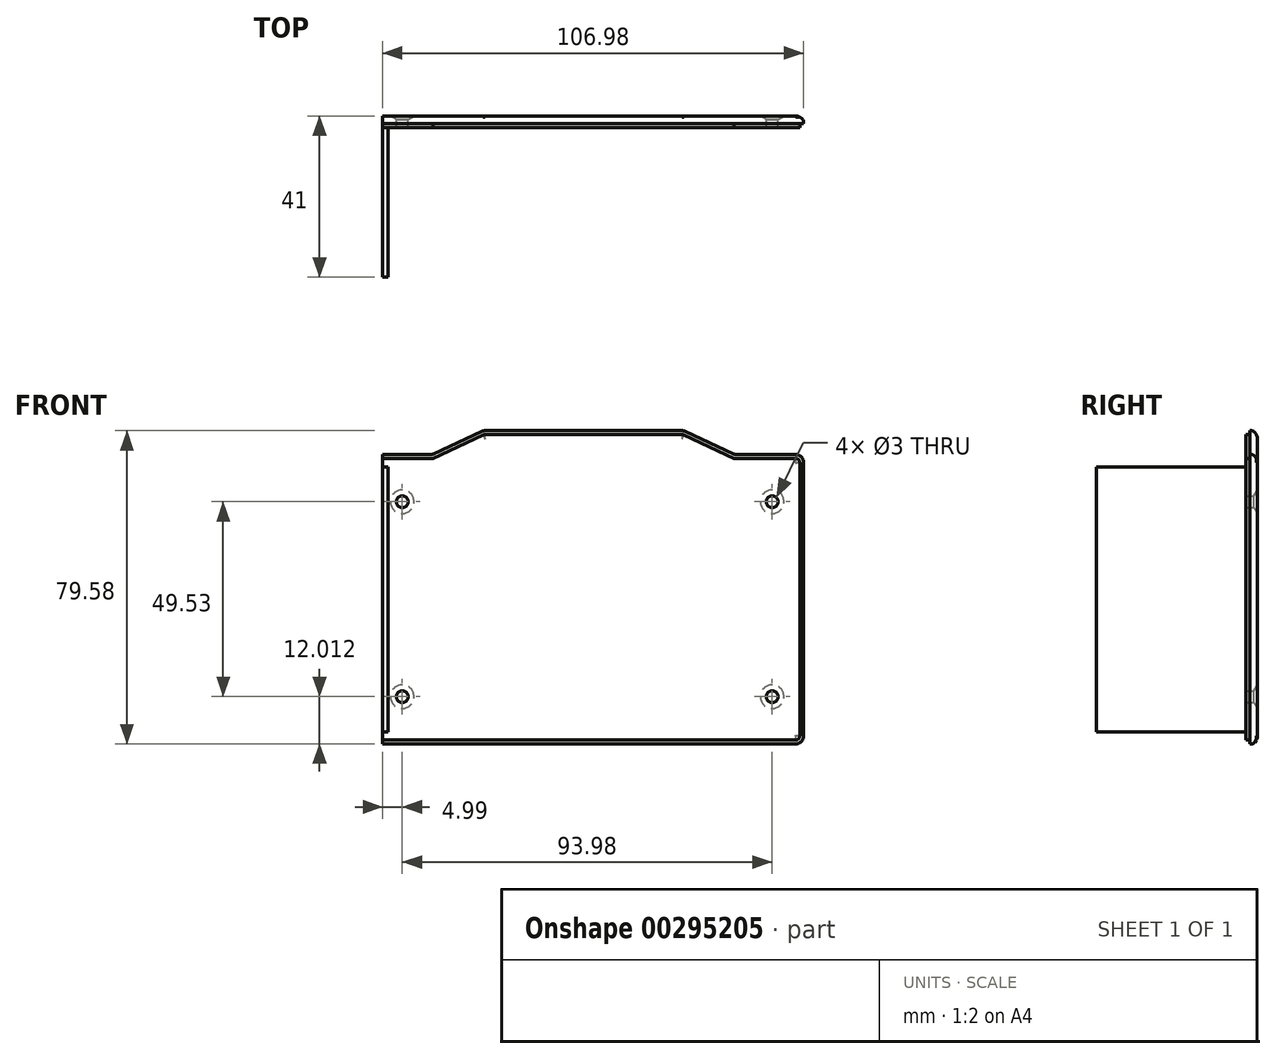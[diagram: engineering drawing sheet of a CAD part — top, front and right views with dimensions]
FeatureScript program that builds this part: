
annotation { "Feature Type Name" : "Feature", "Feature Type Description" : "" }
export const myFeature = defineFeature(function(context is Context, id is Id, definition is map)
    precondition{}
    {
        {
            var Q0;
            Q0=qCreatedBy(makeId("Front.planeOp"),FACE);
            var sketch = newSketch(context, id + "F0", { "sketchPlane" : qUnion([Q0])});
            skLineSegment(sketch, "E0", {"start": v(-120.92, -2) * mm, "end": v(-120.92, -71.52) * mm});
            skLineSegment(sketch, "E1", {"start": v(-118.92, -73.52) * mm, "end": v(-2, -73.52) * mm});
            skLineSegment(sketch, "E2", {"start": v(0, -71.52) * mm, "end": v(0, -2) * mm});
            skLineSegment(sketch, "E3", {"start": v(-81.83, 5.87) * mm, "end": v(-94.02, 0.19) * mm});
            skLineSegment(sketch, "E4", {"start": v(-94.87, 0) * mm, "end": v(-118.92, 0) * mm});
            skLineSegment(sketch, "E5", {"start": v(-2, 0) * mm, "end": v(-16.98, 0) * mm});
            skLineSegment(sketch, "E6", {"start": v(-17.83, 0.19) * mm, "end": v(-30.02, 5.87) * mm});
            skLineSegment(sketch, "E7", {"start": v(-30.87, 6.06) * mm, "end": v(-80.98, 6.06) * mm});
            skPoint(sketch, "E8.visualSharp", {"position": v(0, 0) * mm});
            skArc(sketch, "E8.filletArc", {"start": v(0, -2) * mm, "mid": v(-0.59, -0.59) * mm, "end": v(-2, 0) * mm});
            skPoint(sketch, "E9.visualSharp", {"position": v(-120.92, 0) * mm});
            skArc(sketch, "E9.filletArc", {"start": v(-118.92, 0) * mm, "mid": v(-120.33, -0.59) * mm, "end": v(-120.92, -2) * mm});
            skPoint(sketch, "E10.visualSharp", {"position": v(-120.92, -73.52) * mm});
            skArc(sketch, "E10.filletArc", {"start": v(-120.92, -71.52) * mm, "mid": v(-120.33, -72.93) * mm, "end": v(-118.92, -73.52) * mm});
            skPoint(sketch, "E11.visualSharp", {"position": v(0, -73.52) * mm});
            skArc(sketch, "E11.filletArc", {"start": v(-2, -73.52) * mm, "mid": v(-0.59, -72.93) * mm, "end": v(0, -71.52) * mm});
            skPoint(sketch, "E12.visualSharp", {"position": v(-17.42, 0) * mm});
            skArc(sketch, "E12.filletArc", {"start": v(-17.83, 0.19) * mm, "mid": v(-17.41, 0.05) * mm, "end": v(-16.98, 0) * mm});
            skPoint(sketch, "E13.visualSharp", {"position": v(-30.42, 6.06) * mm});
            skArc(sketch, "E13.filletArc", {"start": v(-30.02, 5.87) * mm, "mid": v(-30.43, 6.01) * mm, "end": v(-30.87, 6.06) * mm});
            skPoint(sketch, "E14.visualSharp", {"position": v(-81.42, 6.06) * mm});
            skArc(sketch, "E14.filletArc", {"start": v(-80.98, 6.06) * mm, "mid": v(-81.41, 6.01) * mm, "end": v(-81.83, 5.87) * mm});
            skPoint(sketch, "E15.visualSharp", {"position": v(-94.42, 0) * mm});
            skArc(sketch, "E15.filletArc", {"start": v(-94.87, 0) * mm, "mid": v(-94.43, 0.05) * mm, "end": v(-94.02, 0.19) * mm});
            skCircle(sketch, "E16", {"center": v(-101.99, -11.98) * mm, "radius": 1.5 * mm});
            skCircle(sketch, "E17", {"center": v(-101.99, -61.5) * mm, "radius": 1.5 * mm});
            skLineSegment(sketch, "E18", {"start": v(-101.99, -11.98) * mm, "end": v(3.2, -11.98) * mm, "construction": true});
            skLineSegment(sketch, "E19", {"start": v(-101.99, -61.5) * mm, "end": v(0.7, -61.5) * mm, "construction": true});
            skCircle(sketch, "E20", {"center": v(-8, -61.5) * mm, "radius": 1.5 * mm});
            skCircle(sketch, "E21", {"center": v(-8, -11.98) * mm, "radius": 1.5 * mm});
            skSolve(sketch);
        }
        {
            var Q0;
            Q0=makeQuery(id+"F0.imprint","IMPRINT",FACE,{"disambiguationData":[TD([[makeQuery(id+"F0.imprint","IMPRINT",EDGE,{"derivedFrom":sQuery(id+"F0.wireOp",EDGE,"E0")}),1.0]])]});
            extrude(context, id + "F1", {"entities" : qUnion([Q0]), "depth" : 2 * mm});
        }
        {
            var Q0;
            Q0=makeQuery(id+"F1.opExtrude","CAP_FACE",FACE,{"disambiguationData":[OSD([sQuery(id+"F0.wireOp",EDGE,"E0"),sQuery(id+"F0.wireOp",EDGE,"E1"),sQuery(id+"F0.wireOp",EDGE,"E2"),sQuery(id+"F0.wireOp",EDGE,"E3"),sQuery(id+"F0.wireOp",EDGE,"E4"),sQuery(id+"F0.wireOp",EDGE,"E5"),sQuery(id+"F0.wireOp",EDGE,"E6"),sQuery(id+"F0.wireOp",EDGE,"E7")])],"isStart":true});
            chamfer(context, id + "F2", {"entities" : qUnion([Q0]), "chamferType" : ChamferType.TWO_OFFSETS, "width1" : 1.5 * mm, "oppositeDirection" : true, "width2" : 1 * mm, "tangentPropagation" : true});
        }
        {
            var Q0;
            {var subQ0=sQuery(id+"F0.wireOp",EDGE,"E7");Q0=makeQuery(id+"F2.opChamfer","BLEND_EDGE",EDGE,{"blendedFrom":[makeQuery(id+"F1.opExtrude","CAP_EDGE",EDGE,{"disambiguationData":[OSD([subQ0])],"isStart":true}),makeQuery(id+"F1.opExtrude","SWEPT_FACE",FACE,{"disambiguationData":[OSD([subQ0])]})],"blendedInto":[makeQuery(id+"F1.opExtrude","SWEPT_FACE",FACE,{"disambiguationData":[OSD([subQ0])]})]});}
            fillet(context, id + "F3", {"entities" : qUnion([Q0]), "radius" : 1 * mm, "tangentPropagation" : true, "allowEdgeOverflow" : false});
        }
        {
            var Q0;
            {var subQ0=sQuery(id+"F0.wireOp",EDGE,"E7");Q0=makeQuery(id+"F2.opChamfer","BLEND_EDGE",EDGE,{"blendedFrom":[makeQuery(id+"F1.opExtrude","CAP_EDGE",EDGE,{"disambiguationData":[OSD([subQ0])],"isStart":true}),makeQuery(id+"F1.opExtrude","CAP_FACE",FACE,{"disambiguationData":[OSD([sQuery(id+"F0.wireOp",EDGE,"E0"),sQuery(id+"F0.wireOp",EDGE,"E1"),sQuery(id+"F0.wireOp",EDGE,"E2"),sQuery(id+"F0.wireOp",EDGE,"E3"),sQuery(id+"F0.wireOp",EDGE,"E4"),sQuery(id+"F0.wireOp",EDGE,"E5"),sQuery(id+"F0.wireOp",EDGE,"E6"),subQ0])],"isStart":true})],"blendedInto":[makeQuery(id+"F1.opExtrude","CAP_FACE",FACE,{"disambiguationData":[OSD([sQuery(id+"F0.wireOp",EDGE,"E0"),sQuery(id+"F0.wireOp",EDGE,"E1"),sQuery(id+"F0.wireOp",EDGE,"E2"),sQuery(id+"F0.wireOp",EDGE,"E3"),sQuery(id+"F0.wireOp",EDGE,"E4"),sQuery(id+"F0.wireOp",EDGE,"E5"),sQuery(id+"F0.wireOp",EDGE,"E6"),subQ0])],"isStart":true})]});}
            fillet(context, id + "F4", {"entities" : qUnion([Q0]), "radius" : 2 * mm, "tangentPropagation" : true, "allowEdgeOverflow" : false});
        }
        {
            var Q0;
            Q0=makeQuery(id+"F1.opExtrude","CAP_FACE",FACE,{"disambiguationData":[OSD([sQuery(id+"F0.wireOp",EDGE,"E0"),sQuery(id+"F0.wireOp",EDGE,"E1"),sQuery(id+"F0.wireOp",EDGE,"E2"),sQuery(id+"F0.wireOp",EDGE,"E3"),sQuery(id+"F0.wireOp",EDGE,"E4"),sQuery(id+"F0.wireOp",EDGE,"E5"),sQuery(id+"F0.wireOp",EDGE,"E6"),sQuery(id+"F0.wireOp",EDGE,"E7"),sQuery(id+"F0.wireOp",EDGE,"E8.filletArc"),sQuery(id+"F0.wireOp",EDGE,"E9.filletArc"),sQuery(id+"F0.wireOp",EDGE,"E10.filletArc"),sQuery(id+"F0.wireOp",EDGE,"E11.filletArc"),sQuery(id+"F0.wireOp",EDGE,"E12.filletArc"),sQuery(id+"F0.wireOp",EDGE,"E13.filletArc"),sQuery(id+"F0.wireOp",EDGE,"E14.filletArc"),sQuery(id+"F0.wireOp",EDGE,"E15.filletArc"),sQuery(id+"F0.wireOp",EDGE,"E16"),sQuery(id+"F0.wireOp",EDGE,"E17"),sQuery(id+"F0.wireOp",EDGE,"E20"),sQuery(id+"F0.wireOp",EDGE,"E21")])],"isStart":false});
            var sketch = newSketch(context, id + "F5", { "sketchPlane" : qUnion([Q0])});
            skLineSegment(sketch, "E22.bottom", {"start": v(-122.92, 2) * mm, "end": v(-106.98, 2) * mm});
            skLineSegment(sketch, "E22.top", {"start": v(-122.92, -75.52) * mm, "end": v(-106.98, -75.52) * mm});
            skLineSegment(sketch, "E22.left", {"start": v(-122.92, 2) * mm, "end": v(-122.92, -75.52) * mm});
            skLineSegment(sketch, "E22.right", {"start": v(-106.98, 2) * mm, "end": v(-106.98, -75.52) * mm});
            skSolve(sketch);
        }
        {
            var Q0;
            {var subQ1=sQuery(id+"F5.wireOp",EDGE,"E22.bottom");Q0=makeQuery(id+"F5.imprint","IMPRINT",FACE,{"disambiguationData":[TD([[makeQuery(id+"F5.imprint","IMPRINT",EDGE,{"derivedFrom":subQ1}),-1.0]])]});}
            var Q1;
            Q1=makeQuery(id+"F5.imprint","IMPRINT",FACE,{"disambiguationData":[TD([[makeQuery(id+"F5.imprint","IMPRINT",EDGE,{"derivedFrom":makeQuery(id+"F1.opExtrude","CAP_EDGE",EDGE,{"disambiguationData":[OSD([sQuery(id+"F0.wireOp",EDGE,"E0")])],"isStart":false})}),1.0]])]});
            extrude(context, id + "F6", {"entities" : qUnion([Q0, Q1]), "operationType" : NewBodyOperationType.REMOVE, "oppositeDirection" : true, "depth" : 25 * mm});
        }
        {
            var Q0;
            Q0=makeQuery(id+"F1.opExtrude","CAP_FACE",FACE,{"disambiguationData":[OSD([sQuery(id+"F0.wireOp",EDGE,"E0"),sQuery(id+"F0.wireOp",EDGE,"E1"),sQuery(id+"F0.wireOp",EDGE,"E2"),sQuery(id+"F0.wireOp",EDGE,"E3"),sQuery(id+"F0.wireOp",EDGE,"E4"),sQuery(id+"F0.wireOp",EDGE,"E5"),sQuery(id+"F0.wireOp",EDGE,"E6"),sQuery(id+"F0.wireOp",EDGE,"E7"),sQuery(id+"F0.wireOp",EDGE,"E8.filletArc"),sQuery(id+"F0.wireOp",EDGE,"E9.filletArc"),sQuery(id+"F0.wireOp",EDGE,"E10.filletArc"),sQuery(id+"F0.wireOp",EDGE,"E11.filletArc"),sQuery(id+"F0.wireOp",EDGE,"E12.filletArc"),sQuery(id+"F0.wireOp",EDGE,"E13.filletArc"),sQuery(id+"F0.wireOp",EDGE,"E14.filletArc"),sQuery(id+"F0.wireOp",EDGE,"E15.filletArc"),sQuery(id+"F0.wireOp",EDGE,"E16"),sQuery(id+"F0.wireOp",EDGE,"E17"),sQuery(id+"F0.wireOp",EDGE,"E20"),sQuery(id+"F0.wireOp",EDGE,"E21")])],"isStart":false});
            var sketch = newSketch(context, id + "F7", { "sketchPlane" : qUnion([Q0])});
            skLineSegment(sketch, "E23.bottom", {"start": v(-106.98, -3.12) * mm, "end": v(-105.65, -3.12) * mm});
            skLineSegment(sketch, "E23.top", {"start": v(-106.98, -70.44) * mm, "end": v(-105.65, -70.44) * mm});
            skLineSegment(sketch, "E23.left", {"start": v(-106.98, -3.12) * mm, "end": v(-106.98, -70.44) * mm});
            skLineSegment(sketch, "E23.right", {"start": v(-105.65, -3.12) * mm, "end": v(-105.65, -70.44) * mm});
            skSolve(sketch);
        }
        {
            var Q0;
            Q0=makeQuery(id+"F7.imprint","IMPRINT",FACE,{"disambiguationData":[TD([[makeQuery(id+"F7.imprint","IMPRINT",EDGE,{"derivedFrom":sQuery(id+"F7.wireOp",EDGE,"E23.bottom")}),-1.0]])]});
            extrude(context, id + "F8", {"entities" : qUnion([Q0]), "operationType" : NewBodyOperationType.ADD, "depth" : 39 * mm});
        }
        {
            var Q0;
            Q0=makeQuery(id+"F1.opExtrude","CAP_FACE",FACE,{"disambiguationData":[OSD([sQuery(id+"F0.wireOp",EDGE,"E0"),sQuery(id+"F0.wireOp",EDGE,"E1"),sQuery(id+"F0.wireOp",EDGE,"E2"),sQuery(id+"F0.wireOp",EDGE,"E3"),sQuery(id+"F0.wireOp",EDGE,"E4"),sQuery(id+"F0.wireOp",EDGE,"E5"),sQuery(id+"F0.wireOp",EDGE,"E6"),sQuery(id+"F0.wireOp",EDGE,"E7"),sQuery(id+"F0.wireOp",EDGE,"E8.filletArc"),sQuery(id+"F0.wireOp",EDGE,"E9.filletArc"),sQuery(id+"F0.wireOp",EDGE,"E10.filletArc"),sQuery(id+"F0.wireOp",EDGE,"E11.filletArc"),sQuery(id+"F0.wireOp",EDGE,"E12.filletArc"),sQuery(id+"F0.wireOp",EDGE,"E13.filletArc"),sQuery(id+"F0.wireOp",EDGE,"E14.filletArc"),sQuery(id+"F0.wireOp",EDGE,"E15.filletArc"),sQuery(id+"F0.wireOp",EDGE,"E16"),sQuery(id+"F0.wireOp",EDGE,"E17"),sQuery(id+"F0.wireOp",EDGE,"E20"),sQuery(id+"F0.wireOp",EDGE,"E21")])],"isStart":false});
            var sketch = newSketch(context, id + "F9", { "sketchPlane" : qUnion([Q0])});
            skLineSegment(sketch, "E24.0", {"start": v(-94.2, -1) * mm, "end": v(-105.98, -1) * mm});
            skLineSegment(sketch, "E24.1", {"start": v(-81.4, 4.97) * mm, "end": v(-94.2, -1) * mm});
            skArc(sketch, "E24.2", {"start": v(-80.98, 5.06) * mm, "mid": v(-81.2, 5.04) * mm, "end": v(-81.4, 4.97) * mm});
            skLineSegment(sketch, "E24.3", {"start": v(-30.87, 5.06) * mm, "end": v(-80.98, 5.06) * mm});
            skArc(sketch, "E24.4", {"start": v(-30.44, 4.97) * mm, "mid": v(-30.65, 5.04) * mm, "end": v(-30.87, 5.06) * mm});
            skLineSegment(sketch, "E24.9", {"start": v(-105.98, -72.52) * mm, "end": v(-2, -72.52) * mm});
            skArc(sketch, "E24.10", {"start": v(-2, -72.52) * mm, "mid": v(-1.3, -72.23) * mm, "end": v(-1, -71.52) * mm});
            skLineSegment(sketch, "E24.11", {"start": v(-1, -71.52) * mm, "end": v(-1, -2) * mm});
            skArc(sketch, "E24.12", {"start": v(-1, -2) * mm, "mid": v(-1.3, -1.3) * mm, "end": v(-2, -1) * mm});
            skLineSegment(sketch, "E24.13", {"start": v(-2, -1) * mm, "end": v(-17.65, -1) * mm});
            skLineSegment(sketch, "E24.14", {"start": v(-105.98, -1) * mm, "end": v(-105.98, -2.12) * mm});
            skLineSegment(sketch, "E24.15", {"start": v(-17.65, -1) * mm, "end": v(-30.44, 4.97) * mm});
            skLineSegment(sketch, "E25", {"start": v(-105.98, -1) * mm, "end": v(-106.98, -1) * mm});
            skLineSegment(sketch, "E26", {"start": v(-105.98, -72.52) * mm, "end": v(-106.98, -72.52) * mm});
            skSolve(sketch);
        }
        {
            var Q0;
            Q0=makeQuery(id+"F9.imprint","IMPRINT",FACE,{"disambiguationData":[TD([[makeQuery(id+"F9.imprint","IMPRINT",EDGE,{"derivedFrom":sQuery(id+"F9.wireOp",EDGE,"E24.0")}),1.0]])]});
            extrude(context, id + "F10", {"entities" : qUnion([Q0]), "operationType" : NewBodyOperationType.ADD, "depth" : 1 * mm});
        }
    });
